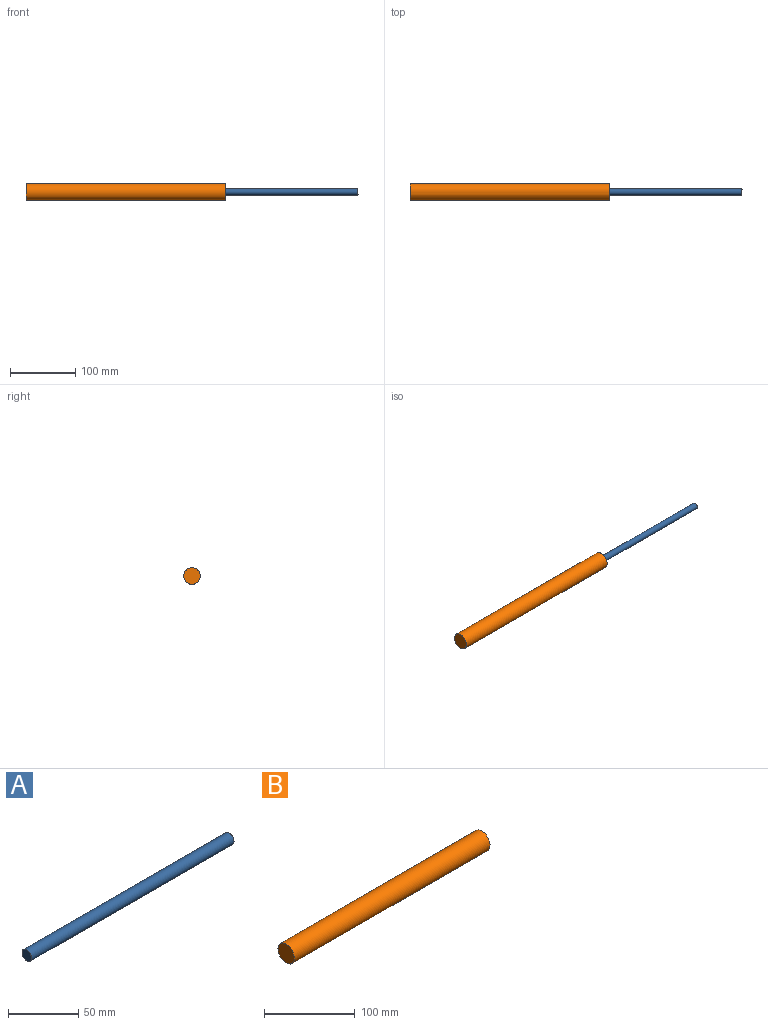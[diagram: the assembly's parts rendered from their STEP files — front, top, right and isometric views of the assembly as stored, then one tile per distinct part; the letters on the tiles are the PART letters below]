
ASSEMBLY  parts=2 mates=1
PART A: 3 faces, bbox 203.2x9.5x9.5 mm
  f0: cylinder r=4.76mm len=203.2mm, axis (-1,0,0), area 6080.5mm2, adj f1,f2
  f1: plane 9.53x9.53mm, normal (1,0,0), area 71.3mm2, adj f0
  f2: plane 9.53x9.53mm, normal (-1,0,0), area 71.3mm2, adj f0
PART B: 3 faces, bbox 304.8x25.4x25.4 mm
  f0: cylinder r=12.7mm len=304.8mm, axis (-1,0,0), area 24322mm2, adj f1,f2
  f1: plane 25.4x25.4mm, normal (1,0,0), area 506.7mm2, adj f0
  f2: plane 25.4x25.4mm, normal (-1,0,0), area 506.7mm2, adj f0
PLACE A rot(axis=(0.96,-0.22,-0.18),0deg) t=(46.21,123.63,-26.78)mm
PLACE B rot(axis=(0.96,-0.22,-0.18),0deg) t=(-258.59,123.63,-26.78)mm
MATE slider B.f0 <-> A.f0  axis (1,0,0) through (46.21,123.63,-26.78)mm
